# Revit family: 306_e04dee84f0b64180a9525deb32477b
name_source: partatom
category: Pipe Accessories
units: mm (PartAtom-declared; Revit-internal decimal feet)

## family parameters
Always vertical = Yes
Cut with Voids When Loaded = No
Part Type = Valve - Breaks Into
Round Connector Dimension = Use Diameter
Shared = No
Work Plane-Based = No

## types (4) — shared parameters
Description = 2-way Motorized ball valve MBA122, PN32 external thread
H1 = 1 mm  [stored 0.00328084 ft]
L2D_Min = 3048 mm
Manufacturer = ESBE
QmdConnectorList = 301;D;302;D
URL = http://www.esbe.eu
X5 = 2 mm  [stored 0.00656168 ft]
X6 = 4 mm  [stored 0.0131234 ft]
X6__ve = -4 mm  [stored -0.0131234 ft]
Y0 = 5 mm  [stored 0.0164042 ft]
Y11 = 3 mm  [stored 0.00984252 ft]
Z3 = 11 mm
Z4 = 52 mm
Z6 = 35 mm
Z6__ve = -35 mm  [stored -0.114829 ft]
Z7 = 3 mm  [stored 0.00984252 ft]
magiPartTypeId = 306
magiProductFamilyId = e04dee84f0b64180a9525deb32477b

## per-type parameters (varying)
- MBA122 G1 ¼  MM 230VAC 2-P 10NM: C=40 mm; D=32 mm; E=29 mm; L2D=70 mm; W2D=32 mm; X1=35 mm; X11=13 mm; X11__ve=-13 mm; X12=22 mm; X12__ve=-22 mm; X14=56 mm; X15=39 mm; X7=6 mm  [stored 0.019685 ft]; X8=27 mm; Y1=14 mm  [stored 0.0459318 ft]; Y10=24 mm  [stored 0.0787402 ft]; Y10__ve=-24 mm  [stored -0.0787402 ft]; Y12=13 mm; Y13=19 mm; Y3=19 mm; Y4=17 mm; Y5=16 mm  [stored 0.0524934 ft]; Z2=26 mm; Z2__ve=-26 mm; Z5=3 mm  [stored 0.00984252 ft]; magiProductCode=MBA122 G1 ¼" MM 230VAC 2-P 10NM; magiProductId=4079d859d7da47e485fe6597663a7a
- MBA122 G3/4  MM 230VAC 2-P 10NM: C=31 mm; D=20 mm; E=22 mm; L2D=50 mm; W2D=20 mm  [stored 0.0656168 ft]; X1=25 mm  [stored 0.082021 ft]; X11=10 mm  [stored 0.0328084 ft]; X11__ve=-10 mm  [stored -0.0328084 ft]; X12=15 mm  [stored 0.0492126 ft]; X12__ve=-15 mm; X14=40 mm; X15=28 mm; X7=5 mm  [stored 0.0164042 ft]; X8=19 mm; Y1=8 mm  [stored 0.0262467 ft]; Y10=15 mm  [stored 0.0492126 ft]; Y10__ve=-15 mm; Y12=8 mm  [stored 0.0262467 ft]; Y13=12 mm  [stored 0.0393701 ft]; Y3=12 mm  [stored 0.0393701 ft]; Y4=11 mm; Y5=10 mm  [stored 0.0328084 ft]; Z2=19 mm; Z2__ve=-19 mm  [stored -0.062336 ft]; Z5=2 mm  [stored 0.00656168 ft]; magiProductCode=MBA122 G3/4" MM 230VAC 2-P 10NM; magiProductId=253f621c2d9f4545bb3b5e7ef32c78
- MBA122 G1  MM 230VAC 2-P 10NM: C=34 mm; D=25 mm; E=25 mm  [stored 0.082021 ft]; L2D=60 mm; W2D=25 mm  [stored 0.082021 ft]; X1=30 mm; X11=11 mm; X11__ve=-11 mm; X12=18 mm  [stored 0.0590551 ft]; X12__ve=-18 mm; X14=48 mm; X15=33 mm; X7=5 mm  [stored 0.0164042 ft]; X8=23 mm; Y1=10 mm  [stored 0.0328084 ft]; Y10=19 mm; Y10__ve=-19 mm  [stored -0.062336 ft]; Y12=10 mm  [stored 0.0328084 ft]; Y13=15 mm  [stored 0.0492126 ft]; Y3=15 mm  [stored 0.0492126 ft]; Y4=14 mm  [stored 0.0459318 ft]; Y5=13 mm; Z2=23 mm; Z2__ve=-23 mm; Z5=3 mm  [stored 0.00984252 ft]; magiProductCode=MBA122 G1" MM 230VAC 2-P 10NM; magiProductId=d9e5a9d5c0504a448c34b385e06f1d
- MBA122 G1 ½  MM 230VAC 2-P 10NM: C=36 mm; D=40 mm; E=34 mm; L2D=74 mm; W2D=40 mm; X1=37 mm; X11=14 mm  [stored 0.0459318 ft]; X11__ve=-14 mm  [stored -0.0459318 ft]; X12=23 mm; X12__ve=-23 mm; X14=59 mm; X15=41 mm; X7=7 mm  [stored 0.0229659 ft]; X8=28 mm; Y1=18 mm  [stored 0.0590551 ft]; Y10=30 mm; Y10__ve=-30 mm; Y12=16 mm  [stored 0.0524934 ft]; Y13=23 mm; Y3=24 mm  [stored 0.0787402 ft]; Y4=22 mm; Y5=20 mm  [stored 0.0656168 ft]; Z2=31 mm; Z2__ve=-31 mm; Z5=3 mm  [stored 0.00984252 ft]; magiProductCode=MBA122 G1 ½" MM 230VAC 2-P 10NM; magiProductId=6202c09f96d640a99dbd5f11f9fdfc

note: [stored X ft] marks values corroborated as IEEE doubles in the binary element streams (Revit-internal decimal feet)

## geometry (parser evidence)
native form markers: Sweep x3
no freeform markers — native parametric forms only
